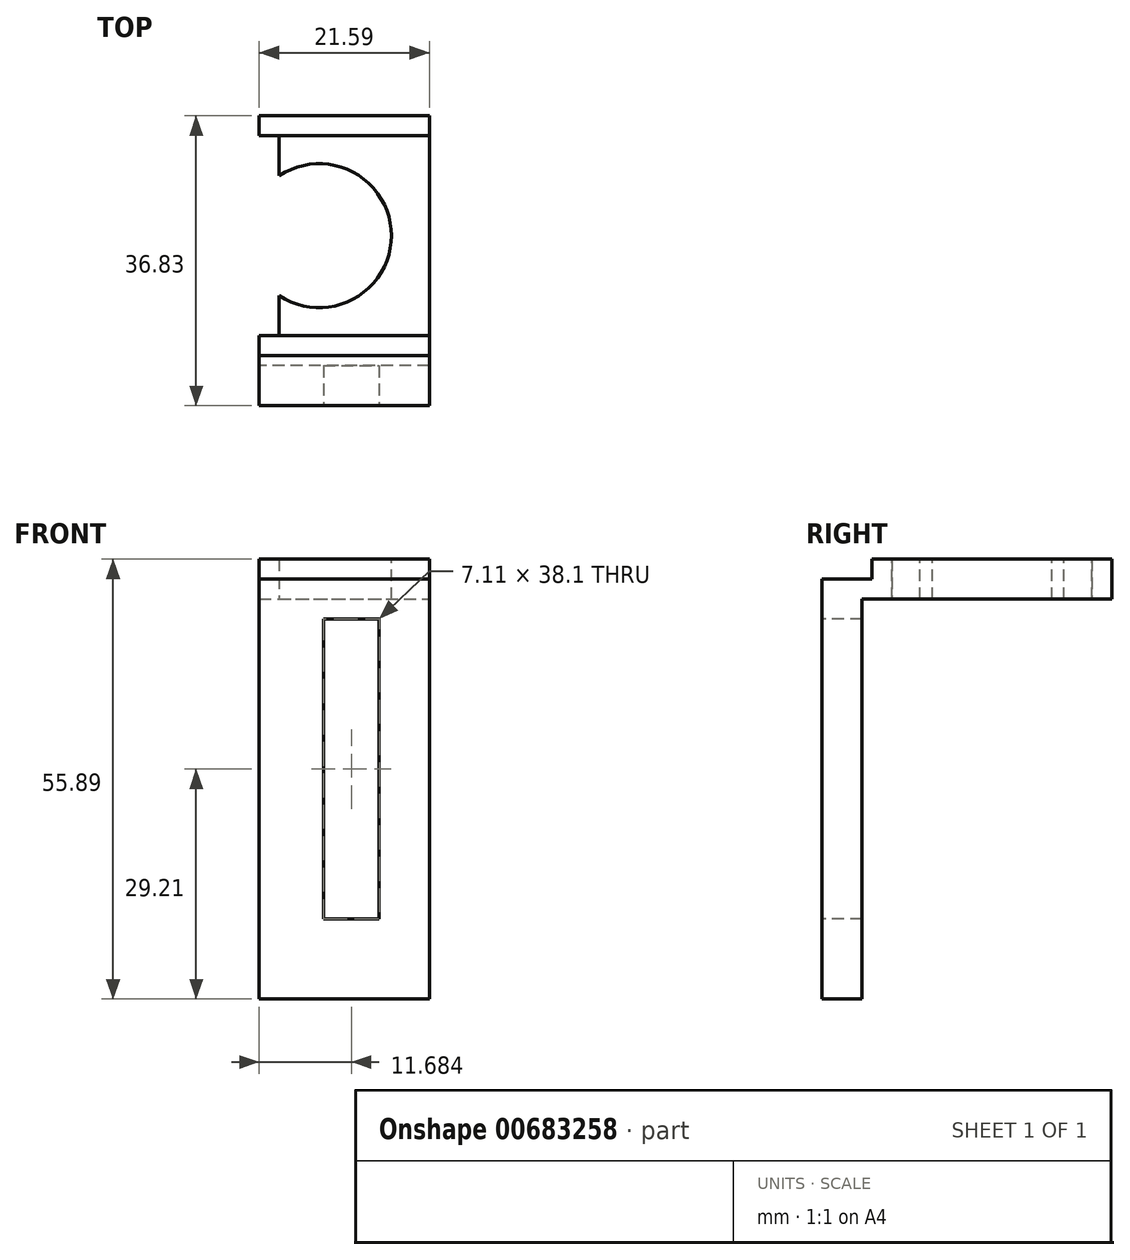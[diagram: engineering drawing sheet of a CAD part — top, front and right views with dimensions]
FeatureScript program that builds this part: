
annotation { "Feature Type Name" : "Feature", "Feature Type Description" : "" }
export const myFeature = defineFeature(function(context is Context, id is Id, definition is map)
    precondition{}
    {
        {
            var Q0;
            Q0=qCreatedBy(makeId("Top.planeOp"),FACE);
            var sketch = newSketch(context, id + "F0", { "sketchPlane" : qUnion([Q0])});
            skLineSegment(sketch, "E0.bottom", {"start": v(0, 25.4) * mm, "end": v(33.02, 25.4) * mm});
            skLineSegment(sketch, "E0.top", {"start": v(0, 0) * mm, "end": v(33.02, 0) * mm});
            skLineSegment(sketch, "E0.left", {"start": v(0, 25.4) * mm, "end": v(0, 0) * mm});
            skLineSegment(sketch, "E0.right", {"start": v(33.02, 25.4) * mm, "end": v(33.02, 0) * mm});
            skSolve(sketch);
        }
        {
            var Q0;
            Q0=makeQuery(id+"F0.imprint","IMPRINT",FACE,{"disambiguationData":[TD([[makeQuery(id+"F0.imprint","IMPRINT",EDGE,{"derivedFrom":sQuery(id+"F0.wireOp",EDGE,"E0.bottom")}),-1.0]])]});
            extrude(context, id + "F1", {"entities" : qUnion([Q0]), "depth" : 5.08 * mm, "offsetDistance" : 25.4 * mm});
        }
        {
            var Q0;
            Q0=makeQuery(id+"F1.opExtrude","CAP_FACE",FACE,{"disambiguationData":[OSD([sQuery(id+"F0.wireOp",EDGE,"E0.bottom"),sQuery(id+"F0.wireOp",EDGE,"E0.top"),sQuery(id+"F0.wireOp",EDGE,"E0.left"),sQuery(id+"F0.wireOp",EDGE,"E0.right")])],"isStart":false});
            var sketch = newSketch(context, id + "F2", { "sketchPlane" : qUnion([Q0])});
            skCircle(sketch, "E1", {"center": v(5.08, 12.7) * mm, "radius": 9.14 * mm});
            skSolve(sketch);
        }
        {
            var Q0;
            Q0=makeQuery(id+"F2.imprint","IMPRINT",FACE,{"disambiguationData":[TD([[makeQuery(id+"F2.imprint","IMPRINT",EDGE,{"derivedFrom":sQuery(id+"F2.wireOp",EDGE,"E1")}),1.0]])]});
            extrude(context, id + "F3", {"entities" : qUnion([Q0]), "operationType" : NewBodyOperationType.REMOVE, "endBound" : BoundingType.THROUGH_ALL, "oppositeDirection" : true, "depth" : 25.4 * mm, "offsetDistance" : 25.4 * mm});
        }
        {
            var Q0;
            Q0=qCreatedBy(makeId("Front.planeOp"),FACE);
            var sketch = newSketch(context, id + "F4", { "sketchPlane" : qUnion([Q0])});
            skLineSegment(sketch, "E2.bottom", {"start": v(-2.54, 0) * mm, "end": v(35.56, 0) * mm});
            skLineSegment(sketch, "E2.top", {"start": v(-2.54, 35.56) * mm, "end": v(35.56, 35.56) * mm});
            skLineSegment(sketch, "E2.left", {"start": v(-2.54, 0) * mm, "end": v(-2.54, 35.56) * mm});
            skLineSegment(sketch, "E2.right", {"start": v(35.56, 0) * mm, "end": v(35.56, 35.56) * mm});
            skSolve(sketch);
        }
        {
            var Q0;
            Q0=makeQuery(id+"F4.imprint","IMPRINT",FACE,{"disambiguationData":[TD([[makeQuery(id+"F4.imprint","IMPRINT",EDGE,{"derivedFrom":sQuery(id+"F4.wireOp",EDGE,"E2.bottom")}),1.0]])]});
            extrude(context, id + "F5", {"entities" : qUnion([Q0]), "operationType" : NewBodyOperationType.ADD, "depth" : 2.54 * mm, "offsetDistance" : 25.4 * mm});
        }
        {
            var Q0;
            Q0=makeQuery(id+"F1.opExtrude","SWEPT_FACE",FACE,{"disambiguationData":[OSD([sQuery(id+"F0.wireOp",EDGE,"E0.bottom")])]});
            var sketch = newSketch(context, id + "F6", { "sketchPlane" : qUnion([Q0])});
            skLineSegment(sketch, "E3.bottom", {"start": v(2.54, 0) * mm, "end": v(-35.56, 0) * mm});
            skLineSegment(sketch, "E3.top", {"start": v(2.54, 35.56) * mm, "end": v(-35.56, 35.56) * mm});
            skLineSegment(sketch, "E3.left", {"start": v(2.54, 0) * mm, "end": v(2.54, 35.56) * mm});
            skLineSegment(sketch, "E3.right", {"start": v(-35.56, 0) * mm, "end": v(-35.56, 35.56) * mm});
            skSolve(sketch);
        }
        {
            var Q0;
            Q0=qSketchRegion(id+"F6",true);
            extrude(context, id + "F7", {"entities" : qUnion([Q0]), "operationType" : NewBodyOperationType.ADD, "depth" : 2.54 * mm, "offsetDistance" : 25.4 * mm});
        }
        {
            var Q0;
            Q0=makeQuery(id+"F7.opExtrude","CAP_FACE",FACE,{"disambiguationData":[OSD([sQuery(id+"F6.wireOp",EDGE,"E3.bottom"),sQuery(id+"F6.wireOp",EDGE,"E3.top"),sQuery(id+"F6.wireOp",EDGE,"E3.left"),sQuery(id+"F6.wireOp",EDGE,"E3.right")])],"isStart":true});
            var sketch = newSketch(context, id + "F8", { "sketchPlane" : qUnion([Q0])});
            skLineSegment(sketch, "E4.bottom", {"start": v(35.56, 35.56) * mm, "end": v(33.02, 35.56) * mm});
            skLineSegment(sketch, "E4.top", {"start": v(35.56, 0) * mm, "end": v(33.02, 0) * mm});
            skLineSegment(sketch, "E4.left", {"start": v(35.56, 35.56) * mm, "end": v(35.56, 0) * mm});
            skLineSegment(sketch, "E4.right", {"start": v(33.02, 35.56) * mm, "end": v(33.02, 0) * mm});
            skSolve(sketch);
        }
        {
            var Q0;
            {var subQ2=sQuery(id+"F8.wireOp",EDGE,"E4.bottom");Q0=makeQuery(id+"F8.imprint","IMPRINT",FACE,{"disambiguationData":[TD([[makeQuery(id+"F8.imprint","IMPRINT",EDGE,{"derivedFrom":subQ2}),-1.0]])]});}
            var Q1;
            Q1=makeQuery(id+"F5.opExtrude","CAP_FACE",FACE,{"disambiguationData":[OSD([sQuery(id+"F4.wireOp",EDGE,"E2.bottom"),sQuery(id+"F4.wireOp",EDGE,"E2.top"),sQuery(id+"F4.wireOp",EDGE,"E2.left"),sQuery(id+"F4.wireOp",EDGE,"E2.right")])],"isStart":true});
            extrude(context, id + "F9", {"entities" : qUnion([Q0]), "operationType" : NewBodyOperationType.ADD, "endBound" : BoundingType.UP_TO_SURFACE, "depth" : 25.4 * mm, "endBoundEntityFace" : qUnion([Q1]), "offsetDistance" : 25.4 * mm});
        }
        {
            var Q0;
            Q0=makeQuery(id+"F9.boolean.opBoolean","MERGE",FACE,{"derivedFrom":[makeQuery(id+"F5.opExtrude","SWEPT_FACE",FACE,{"disambiguationData":[OSD([sQuery(id+"F4.wireOp",EDGE,"E2.top")])]}),makeQuery(id+"F7.opExtrude","SWEPT_FACE",FACE,{"disambiguationData":[OSD([sQuery(id+"F6.wireOp",EDGE,"E3.top")])]}),makeQuery(id+"F9.opExtrude","SWEPT_FACE",FACE,{"disambiguationData":[OSD([sQuery(id+"F8.wireOp",EDGE,"E4.bottom")])]})]});
            var sketch = newSketch(context, id + "F10", { "sketchPlane" : qUnion([Q0])});
            skLineSegment(sketch, "E5.bottom", {"start": v(35.56, 27.94) * mm, "end": v(-2.54, 27.94) * mm});
            skLineSegment(sketch, "E5.top", {"start": v(35.56, -2.54) * mm, "end": v(-2.54, -2.54) * mm});
            skLineSegment(sketch, "E5.left", {"start": v(35.56, 27.94) * mm, "end": v(35.56, -2.54) * mm});
            skLineSegment(sketch, "E5.right", {"start": v(-2.54, 27.94) * mm, "end": v(-2.54, -2.54) * mm});
            skLineSegment(sketch, "E6.bottom", {"start": v(24.13, 17.6) * mm, "end": v(21.6, 17.6) * mm});
            skLineSegment(sketch, "E6.top", {"start": v(24.13, 7.44) * mm, "end": v(21.6, 7.44) * mm});
            skLineSegment(sketch, "E6.left", {"start": v(24.13, 17.6) * mm, "end": v(24.13, 7.44) * mm});
            skLineSegment(sketch, "E6.right", {"start": v(21.6, 17.6) * mm, "end": v(21.6, 7.44) * mm});
            skSolve(sketch);
        }
        {
            var Q0;
            Q0=makeQuery(id+"F10.imprint","IMPRINT",FACE,{"disambiguationData":[TD([[makeQuery(id+"F10.imprint","IMPRINT",EDGE,{"derivedFrom":sQuery(id+"F10.wireOp",EDGE,"E6.bottom")}),-1.0]])]});
            var Q1;
            {var subQ5=sQuery(id+"F10.wireOp",EDGE,"E5.bottom");Q1=makeQuery(id+"F10.imprint","IMPRINT",FACE,{"disambiguationData":[TD([[makeQuery(id+"F10.imprint","IMPRINT",EDGE,{"derivedFrom":subQ5}),-1.0]])]});}
            extrude(context, id + "F11", {"entities" : qUnion([Q0, Q1]), "depth" : 2.54 * mm, "offsetDistance" : 25.4 * mm});
        }
        {
            var Q0;
            Q0=makeQuery(id+"F5.opExtrude","CAP_FACE",FACE,{"disambiguationData":[OSD([sQuery(id+"F4.wireOp",EDGE,"E2.bottom"),sQuery(id+"F4.wireOp",EDGE,"E2.top"),sQuery(id+"F4.wireOp",EDGE,"E2.left"),sQuery(id+"F4.wireOp",EDGE,"E2.right")])],"isStart":false});
            var sketch = newSketch(context, id + "F12", { "sketchPlane" : qUnion([Q0])});
            skLineSegment(sketch, "E7.bottom", {"start": v(35.56, 0) * mm, "end": v(-2.54, 0) * mm});
            skLineSegment(sketch, "E7.top", {"start": v(35.56, 2.54) * mm, "end": v(-2.54, 2.54) * mm});
            skLineSegment(sketch, "E7.left", {"start": v(35.56, 0) * mm, "end": v(35.56, 2.54) * mm});
            skLineSegment(sketch, "E7.right", {"start": v(-2.54, 0) * mm, "end": v(-2.54, 2.54) * mm});
            skSolve(sketch);
        }
        {
            var Q0;
            Q0=makeQuery(id+"F12.imprint","IMPRINT",FACE,{"disambiguationData":[TD([[makeQuery(id+"F12.imprint","IMPRINT",EDGE,{"derivedFrom":sQuery(id+"F12.wireOp",EDGE,"E7.bottom")}),1.0]])]});
            extrude(context, id + "F13", {"entities" : qUnion([Q0]), "operationType" : NewBodyOperationType.ADD, "depth" : 6.35 * mm, "offsetDistance" : 25.4 * mm});
        }
        {
            var Q0;
            Q0=makeQuery(id+"F13.boolean.opBoolean","MERGE",FACE,{"derivedFrom":[makeQuery(id+"F9.boolean.opBoolean","MERGE",FACE,{"derivedFrom":[makeQuery(id+"F7.boolean.opBoolean","MERGE",FACE,{"derivedFrom":[makeQuery(id+"F5.boolean.opBoolean","MERGE",FACE,{"derivedFrom":[makeQuery(id+"F1.opExtrude","CAP_FACE",FACE,{"disambiguationData":[OSD([sQuery(id+"F0.wireOp",EDGE,"E0.bottom"),sQuery(id+"F0.wireOp",EDGE,"E0.top"),sQuery(id+"F0.wireOp",EDGE,"E0.left"),sQuery(id+"F0.wireOp",EDGE,"E0.right")])],"isStart":true}),makeQuery(id+"F5.opExtrude","SWEPT_FACE",FACE,{"disambiguationData":[OSD([sQuery(id+"F4.wireOp",EDGE,"E2.bottom")])]})]}),makeQuery(id+"F7.opExtrude","SWEPT_FACE",FACE,{"disambiguationData":[OSD([sQuery(id+"F6.wireOp",EDGE,"E3.bottom")])]})]}),makeQuery(id+"F9.opExtrude","SWEPT_FACE",FACE,{"disambiguationData":[OSD([sQuery(id+"F8.wireOp",EDGE,"E4.top")])]})]}),makeQuery(id+"F13.opExtrude","SWEPT_FACE",FACE,{"disambiguationData":[OSD([sQuery(id+"F12.wireOp",EDGE,"E7.bottom")])]})]});
            var sketch = newSketch(context, id + "F14", { "sketchPlane" : qUnion([Q0])});
            skLineSegment(sketch, "E8.bottom", {"start": v(35.56, 8.9) * mm, "end": v(-2.54, 8.9) * mm});
            skLineSegment(sketch, "E8.top", {"start": v(35.56, 3.81) * mm, "end": v(-2.54, 3.81) * mm});
            skLineSegment(sketch, "E8.left", {"start": v(35.56, 8.9) * mm, "end": v(35.56, 3.81) * mm});
            skLineSegment(sketch, "E8.right", {"start": v(-2.54, 8.9) * mm, "end": v(-2.54, 3.81) * mm});
            skSolve(sketch);
        }
        {
            var Q0;
            Q0=makeQuery(id+"F14.imprint","IMPRINT",FACE,{"disambiguationData":[TD([[makeQuery(id+"F14.imprint","IMPRINT",EDGE,{"derivedFrom":sQuery(id+"F14.wireOp",EDGE,"E8.bottom")}),-1.0]])]});
            extrude(context, id + "F15", {"entities" : qUnion([Q0]), "operationType" : NewBodyOperationType.ADD, "depth" : 50.8 * mm, "offsetDistance" : 25.4 * mm});
        }
        {
            var Q0;
            Q0=makeQuery(id+"F15.boolean.opBoolean","MERGE",FACE,{"derivedFrom":[makeQuery(id+"F13.opExtrude","CAP_FACE",FACE,{"disambiguationData":[OSD([sQuery(id+"F12.wireOp",EDGE,"E7.bottom"),sQuery(id+"F12.wireOp",EDGE,"E7.top"),sQuery(id+"F12.wireOp",EDGE,"E7.left"),sQuery(id+"F12.wireOp",EDGE,"E7.right")])],"isStart":false}),makeQuery(id+"F15.opExtrude","SWEPT_FACE",FACE,{"disambiguationData":[OSD([sQuery(id+"F14.wireOp",EDGE,"E8.bottom")])]})]});
            var sketch = newSketch(context, id + "F16", { "sketchPlane" : qUnion([Q0])});
            skLineSegment(sketch, "E9.bottom", {"start": v(12.7, -2.54) * mm, "end": v(5.59, -2.54) * mm});
            skLineSegment(sketch, "E9.top", {"start": v(12.7, -40.64) * mm, "end": v(5.59, -40.64) * mm});
            skLineSegment(sketch, "E9.left", {"start": v(12.7, -2.54) * mm, "end": v(12.7, -40.64) * mm});
            skLineSegment(sketch, "E9.right", {"start": v(5.59, -2.54) * mm, "end": v(5.59, -40.64) * mm});
            skSolve(sketch);
        }
        {
            var Q0;
            Q0=makeQuery(id+"F16.imprint","IMPRINT",FACE,{"disambiguationData":[TD([[makeQuery(id+"F16.imprint","IMPRINT",EDGE,{"derivedFrom":sQuery(id+"F16.wireOp",EDGE,"E9.bottom")}),1.0]])]});
            extrude(context, id + "F17", {"entities" : qUnion([Q0]), "operationType" : NewBodyOperationType.REMOVE, "oppositeDirection" : true, "depth" : 25.4 * mm, "offsetDistance" : 25.4 * mm});
        }
        {
            var Q0;
            Q0=makeQuery(id+"F1.opExtrude","SWEPT_BODY",BODY,{"disambiguationData":[OSD([sQuery(id+"F0.wireOp",EDGE,"E0.bottom"),sQuery(id+"F0.wireOp",EDGE,"E0.top"),sQuery(id+"F0.wireOp",EDGE,"E0.left"),sQuery(id+"F0.wireOp",EDGE,"E0.right")])]});
            var Q1;
            Q1=makeQuery(id+"F11.opExtrude","SWEPT_BODY",BODY,{"disambiguationData":[OSD([sQuery(id+"F10.wireOp",EDGE,"E5.bottom"),sQuery(id+"F10.wireOp",EDGE,"E5.top"),sQuery(id+"F10.wireOp",EDGE,"E5.left"),sQuery(id+"F10.wireOp",EDGE,"E5.right"),sQuery(id+"F10.wireOp",EDGE,"E6.bottom"),sQuery(id+"F10.wireOp",EDGE,"E6.top"),sQuery(id+"F10.wireOp",EDGE,"E6.left"),sQuery(id+"F10.wireOp",EDGE,"E6.right")])]});
            booleanBodies(context, id + "F18", {"operationType" : BooleanOperationType.UNION, "tools" : qUnion([Q0, Q1])});
        }
        {
            var Q0;
            Q0=makeQuery(id+"F18.opBoolean","MERGE",FACE,{"derivedFrom":[makeQuery(id+"F7.opExtrude","CAP_FACE",FACE,{"disambiguationData":[OSD([sQuery(id+"F6.wireOp",EDGE,"E3.bottom"),sQuery(id+"F6.wireOp",EDGE,"E3.top"),sQuery(id+"F6.wireOp",EDGE,"E3.left"),sQuery(id+"F6.wireOp",EDGE,"E3.right")])],"isStart":false}),makeQuery(id+"F11.opExtrude","SWEPT_FACE",FACE,{"disambiguationData":[OSD([sQuery(id+"F10.wireOp",EDGE,"E5.bottom")])]})]});
            var sketch = newSketch(context, id + "F19", { "sketchPlane" : qUnion([Q0])});
            skLineSegment(sketch, "E10.bottom", {"start": v(-19.05, 38.1) * mm, "end": v(-57, 38.1) * mm});
            skLineSegment(sketch, "E10.top", {"start": v(-19.05, -76.6) * mm, "end": v(-57, -76.6) * mm});
            skLineSegment(sketch, "E10.left", {"start": v(-19.05, 38.1) * mm, "end": v(-19.05, -76.6) * mm});
            skLineSegment(sketch, "E10.right", {"start": v(-57, 38.1) * mm, "end": v(-57, -76.6) * mm});
            skSolve(sketch);
        }
        {
            var Q0;
            Q0 = qSketchRegion(id + "F19", true);
            extrude(context, id + "F20", {"entities" : qUnion([Q0]), "operationType" : NewBodyOperationType.REMOVE, "endBound" : BoundingType.THROUGH_ALL, "oppositeDirection" : true, "depth" : 25.4 * mm, "offsetDistance" : 25.4 * mm});
        }
        {
            var Q0;
            Q0=makeQuery(id+"F18.opBoolean","MERGE",FACE,{"derivedFrom":[makeQuery(id+"F7.opExtrude","SWEPT_FACE",FACE,{"disambiguationData":[OSD([sQuery(id+"F6.wireOp",EDGE,"E3.left")])]}),makeQuery(id+"F11.opExtrude","SWEPT_FACE",FACE,{"disambiguationData":[OSD([sQuery(id+"F10.wireOp",EDGE,"E5.right")])]}),makeQuery(id+"F15.boolean.opBoolean","MERGE",FACE,{"derivedFrom":[makeQuery(id+"F13.boolean.opBoolean","MERGE",FACE,{"derivedFrom":[makeQuery(id+"F5.opExtrude","SWEPT_FACE",FACE,{"disambiguationData":[OSD([sQuery(id+"F4.wireOp",EDGE,"E2.left")])]}),makeQuery(id+"F13.opExtrude","SWEPT_FACE",FACE,{"disambiguationData":[OSD([sQuery(id+"F12.wireOp",EDGE,"E7.right")])]})]}),makeQuery(id+"F15.opExtrude","SWEPT_FACE",FACE,{"disambiguationData":[OSD([sQuery(id+"F14.wireOp",EDGE,"E8.right")])]})]})]});
            var sketch = newSketch(context, id + "F21", { "sketchPlane" : qUnion([Q0])});
            skLineSegment(sketch, "E11.bottom", {"start": v(2.54, 5.1) * mm, "end": v(-27.94, 5.1) * mm});
            skLineSegment(sketch, "E11.top", {"start": v(2.54, 38.1) * mm, "end": v(-27.94, 38.1) * mm});
            skLineSegment(sketch, "E11.left", {"start": v(2.54, 5.1) * mm, "end": v(2.54, 38.1) * mm});
            skLineSegment(sketch, "E11.right", {"start": v(-27.94, 5.1) * mm, "end": v(-27.94, 38.1) * mm});
            skSolve(sketch);
        }
        {
            var Q0;
            Q0=makeQuery(id+"F21.imprint","IMPRINT",FACE,{"disambiguationData":[TD([[makeQuery(id+"F21.imprint","IMPRINT",EDGE,{"derivedFrom":sQuery(id+"F21.wireOp",EDGE,"E11.top")}),-1.0]])]});
            extrude(context, id + "F22", {"entities" : qUnion([Q0]), "operationType" : NewBodyOperationType.REMOVE, "endBound" : BoundingType.THROUGH_ALL, "oppositeDirection" : true, "depth" : 25.4 * mm, "offsetDistance" : 25.4 * mm});
        }
    });
